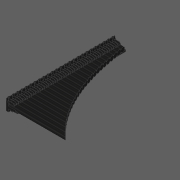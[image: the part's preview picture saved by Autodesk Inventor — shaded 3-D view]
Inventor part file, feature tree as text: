
AUTODESK INVENTOR PART (.ipt)
format: ipt  version: 2020 (Build 240168000, 168)  size: 2,519,552 bytes
history: native  units: in
note: dims shown in document units (in); Inventor stores cm internally (conversion verified against a paired STEP export)
features: other x24, extrude x15, pattern_linear x3, loft x2, fillet x1, sketch x1
ambient origin geometry x8: Origin, YZ Plane, XZ Plane, XY Plane, X Axis, Y Axis, Z Axis, Center Point
bodies: Solid1 (feature_tree)
feature tree (46):
  other  "CrossSection1"
  other  "Vertical Midplane"
  other  "Horizontal Midplane"
  extrude  "Block"  Depth=11.8307in
  extrude  "Hinge Protrusion"  Depth=11.8307in TaperAngle=0.0deg
  other  "Resonator Profile"
  extrude  "Resonator"  Depth=11.8307in
  extrude  "Resonator Cut"  TaperAngle=0.0deg  [1 undecoded]
  extrude  "Duct Cavity"  Depth=11.8307in
  other  "Duct Entrance Loft Plane"
  loft  "Duct Entrance"
  other  "Fitting"
  extrude  "Slit"  Depth=11.8307in
  extrude  "Edge Cut"  Depth=11.8307in
  other  "Edge Plane"
  other  "Edge Sketch"
  loft  "Edge Loft"
  extrude  "Edge"  Depth=11.8307in
  other  "Edge Cut Plane"
  pattern_linear  "Channel Repetition"  Spacing1=0.5512in  [1 undecoded]
  extrude  "Edge Length Cut"  Depth=0.2362in TaperAngle=0.0deg
  other  "Tube Length Curve"
  extrude  "Tube Length Cut"  Depth=0.2461in
  extrude  "Whistle Walls"  Depth=11.8307in
  fillet  "Whistle Wall Fillet"  Radius=0.1245in
  pattern_linear  "Whistle Wall Repetition"  Spacing1=0.1528in  [1 undecoded]
  other  "End Cap Tidying Plane"
  other  "End Cap Tidying Sketch"
  extrude  "End Caps"  Depth=0.2461in
  extrude  "End Cap Tidying"  Depth=0.3937in
  extrude  "Block Fix"  Depth=0.2362in TaperAngle=0.0deg
  pattern_linear  "End Cap Tidying Repetition"  Spacing1=0.0197in  [1 undecoded]
  extrude  "End Cap Tidying (edges)"  Depth=11.8307in
  other  "Block Profile"
  other  "Fitting Sketch"
  other  "Duct Cavity Profile"
  other  "Duct Entrance Loft From"
  other  "Slit Sketch"
  other  "Hinge Protrusion Sketch"
  other  "Edge Cut Sketch"
  other  "Edges3"
  other  "Edge Length Curve"
  sketch  "Sketch19"  dims[d6=0.0in d7=9.8425in d9=0.4724in d20=0.3153in d21=0.0in d58=0.4921in d59=0.0in d61=0.4921in d62=2.3498in d63=0.0in d70=0.1969in d71=0.1292in d80=90.0deg d100=0.2151in d104=0.5512in d105=0.2362in d106=0.0in d109=0.2461in d111=0.1528in d112=0.1245in d114=0.1528in d115=0.2461in d118=0.3937in d141=0.2362in d142=0.0in d148=0.0197in d150=0.2559in d151=0.8858in d152=0.4921in d154=0.0in d160=0.1969in d161=0.0in d162=0.2461in d163=0.2362in d165=0.2461in d166=0.2461in d167=0.0in d171=0.2362in d174=0.4921in d175=0.4528in d176=0.0in d177=90.0deg d178=0.0in d179=90.0deg d185=0.3273in d186=0.0in d189=0.1931in d190=28.3465in d191=38.2054in d198=0.0803in d199=0.0in d200=0.0197in d201=0.0787in d202=-0.125in d203=0.7874in d206=0.2559in d207=0.5241in d209=0.0in d211=9.8425in d213=0.4724in d214=0.2362in d216=0.4528in d217=0.4921in d222=0.0394in d223=0.8058in d229=0.4921in d230=0.0in d234=0.4724in d235=0.4921in d237=0.2461in d239=1.4483in d240=0.0in d241=9.8425in d243=0.4724in d246=0.0394in d247=0.7043in d248=0.0in d249=0.2461in d250=11.8209in d251=0.0098in d252=28.3465in d253=38.2054in d254=28.3465in d255=38.2054in d256=-0.1181in d257=0.2362in d258=0.2151in d259=0.2461in d260=0.1245in d261=0.0in d262=90.0deg d263=0.0in d264=90.0deg d265=11.8307in d266=6.2114in d267=0.9843in d268=0.0in d137=0.0197in d138=0.0344in d139=0.0197in d140=0.0344in d208=0.0197in d269=0.0197in d270=0.0344in]
  other  "2D Equation Curve10"
  other  "2D Equation Curve11"
  other  "Duct Entrance Loft To"
note: 4 required parameter values undecoded (feature->parameter linkage not recoverable at this tier; creation-order binding heuristic only, values carry confidence <= 0.55)
